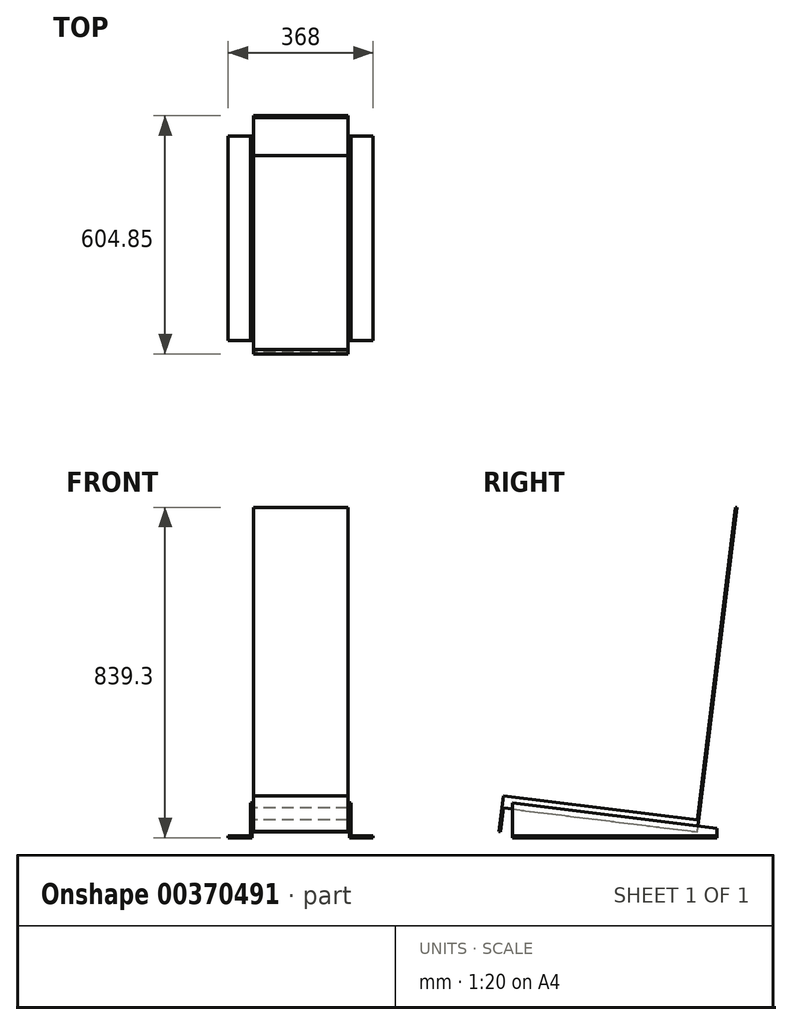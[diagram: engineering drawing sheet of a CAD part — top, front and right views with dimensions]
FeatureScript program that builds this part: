
annotation { "Feature Type Name" : "Feature", "Feature Type Description" : "" }
export const myFeature = defineFeature(function(context is Context, id is Id, definition is map)
    precondition{}
    {
        {
            var Q0;
            Q0=qCreatedBy(makeId("Right.planeOp"),FACE);
            var sketch = newSketch(context, id + "F0", { "sketchPlane" : qUnion([Q0])});
            skLineSegment(sketch, "E0", {"start": v(0, 0) * mm, "end": v(3.66, 29.78) * mm});
            skLineSegment(sketch, "E1", {"start": v(-492.62, 90.71) * mm, "end": v(-503.7, 0.49) * mm});
            skLineSegment(sketch, "E2", {"start": v(-503.7, 0.49) * mm, "end": v(-499.72, 0) * mm});
            skLineSegment(sketch, "E3", {"start": v(-499.72, 0) * mm, "end": v(-492.3, 60.45) * mm});
            skLineSegment(sketch, "E4", {"start": v(-492.3, 60.45) * mm, "end": v(0, 0) * mm});
            skLineSegment(sketch, "E5", {"start": v(-492.62, 90.71) * mm, "end": v(3.66, 29.78) * mm});
            skSolve(sketch);
        }
        {
            var Q0;
            Q0 = qSketchRegion(id + "F0", true);
            extrude(context, id + "F1", {"entities" : qUnion([Q0]), "depth" : 120 * mm});
        }
        {
            var Q0;
            Q0=makeQuery(id+"F1.opExtrude","CAP_FACE",FACE,{"disambiguationData":[OSD([sQuery(id+"F0.wireOp",EDGE,"E0"),sQuery(id+"F0.wireOp",EDGE,"E1"),sQuery(id+"F0.wireOp",EDGE,"E2"),sQuery(id+"F0.wireOp",EDGE,"E3"),sQuery(id+"F0.wireOp",EDGE,"E4"),sQuery(id+"F0.wireOp",EDGE,"E5")])],"isStart":false});
            var sketch = newSketch(context, id + "F2", { "sketchPlane" : qUnion([Q0])});
            skLineSegment(sketch, "E6", {"start": v(50, -15) * mm, "end": v(-470, -15) * mm});
            skLineSegment(sketch, "E7", {"start": v(-470, -15) * mm, "end": v(-470, 72.82) * mm});
            skLineSegment(sketch, "E8", {"start": v(-470, 72.82) * mm, "end": v(50, 8.97) * mm});
            skLineSegment(sketch, "E9", {"start": v(50, 8.97) * mm, "end": v(50, -15) * mm});
            skSolve(sketch);
        }
        {
            var Q0;
            {var subQ5=sQuery(id+"F2.wireOp",EDGE,"E6");Q0=makeQuery(id+"F2.imprint","IMPRINT",FACE,{"disambiguationData":[TD([[makeQuery(id+"F2.imprint","IMPRINT",EDGE,{"derivedFrom":subQ5}),-1.0]])]});}
            var Q1;
            {var subQ0=sQuery(id+"F2.wireOp",EDGE,"E8");var subQ1=sQuery(id+"F2.wireOp",EDGE,"E7");var subQ2=makeQuery(id+"F2.imprint","INTERSECT",VERTEX,{"derivedFrom":[subQ1,subQ0]});Q1=makeQuery(id+"F2.imprint","IMPRINT",FACE,{"disambiguationData":[TD([[makeQuery(id+"F2.imprint","IMPRINT",EDGE,{"disambiguationData":[TD([[subQ2,1.0]])],"derivedFrom":subQ1}),-1.0]])]});}
            extrude(context, id + "F3", {"entities" : qUnion([Q0, Q1]), "depth" : 60 * mm});
        }
        {
            var Q0;
            Q0=makeQuery(id+"F3.opExtrude","SWEPT_BODY",BODY,{"disambiguationData":[OSD([sQuery(id+"F2.wireOp",EDGE,"E6"),sQuery(id+"F2.wireOp",EDGE,"E7"),sQuery(id+"F2.wireOp",EDGE,"E8"),sQuery(id+"F2.wireOp",EDGE,"E9")])]});
            transform(context, id + "F4", {"entities" : qUnion([Q0]), "transformType" : TransformType.TRANSLATION_3D, "dx" : 4 * mm, "dy" : 0 * mm, "dz" : 0 * mm, "makeCopy" : false});
        }
        {
            var Q0;
            Q0=makeQuery(id+"F3.opExtrude","SWEPT_FACE",FACE,{"disambiguationData":[OSD([sQuery(id+"F2.wireOp",EDGE,"E7")])]});
            var Q1;
            Q1=makeQuery(id+"F3.opExtrude","CAP_FACE",FACE,{"disambiguationData":[OSD([sQuery(id+"F2.wireOp",EDGE,"E6"),sQuery(id+"F2.wireOp",EDGE,"E7"),sQuery(id+"F2.wireOp",EDGE,"E8"),sQuery(id+"F2.wireOp",EDGE,"E9")])],"isStart":false});
            var Q2;
            Q2=makeQuery(id+"F3.opExtrude","SWEPT_FACE",FACE,{"disambiguationData":[OSD([sQuery(id+"F2.wireOp",EDGE,"E8")])]});
            var Q3;
            Q3=makeQuery(id+"F3.opExtrude","SWEPT_FACE",FACE,{"disambiguationData":[OSD([sQuery(id+"F2.wireOp",EDGE,"E9")])]});
            shell(context, id + "F5", {"entities" : qUnion([Q0, Q1, Q2, Q3]), "thickness" : 4 * mm});
        }
        {
            var Q0;
            Q0=makeQuery(id+"F1.opExtrude","SWEPT_FACE",FACE,{"disambiguationData":[OSD([sQuery(id+"F0.wireOp",EDGE,"E5")])]});
            var sketch = newSketch(context, id + "F6", { "sketchPlane" : qUnion([Q0])});
            skLineSegment(sketch, "E10.bottom", {"start": v(120, 0) * mm, "end": v(0, 0) * mm});
            skLineSegment(sketch, "E10.top", {"start": v(120, -4) * mm, "end": v(0, -4) * mm});
            skLineSegment(sketch, "E10.left", {"start": v(120, 0) * mm, "end": v(120, -4) * mm});
            skLineSegment(sketch, "E10.right", {"start": v(0, 0) * mm, "end": v(0, -4) * mm});
            skSolve(sketch);
        }
        {
            var Q0;
            Q0 = qSketchRegion(id + "F6", true);
            extrude(context, id + "F7", {"entities" : qUnion([Q0]), "operationType" : NewBodyOperationType.ADD, "depth" : 800 * mm});
        }
        {
            var Q0;
            {var subQ0=sQuery(id+"F2.wireOp",EDGE,"E8");var subQ1=sQuery(id+"F2.wireOp",EDGE,"E7");var subQ2=makeQuery(id+"F2.imprint","INTERSECT",VERTEX,{"derivedFrom":[subQ1,subQ0]});Q0=makeQuery(id+"F2.imprint","IMPRINT",FACE,{"disambiguationData":[TD([[makeQuery(id+"F2.imprint","IMPRINT",EDGE,{"disambiguationData":[TD([[subQ2,1.0]])],"derivedFrom":subQ1}),-1.0]])]});}
            extrude(context, id + "F8", {"entities" : qUnion([Q0]), "depth" : 4 * mm});
        }
        {
            var Q0;
            Q0=makeQuery(id+"F3.opExtrude","SWEPT_BODY",BODY,{"disambiguationData":[OSD([sQuery(id+"F2.wireOp",EDGE,"E6"),sQuery(id+"F2.wireOp",EDGE,"E7"),sQuery(id+"F2.wireOp",EDGE,"E8"),sQuery(id+"F2.wireOp",EDGE,"E9")])]});
            var Q1;
            Q1=makeQuery(id+"F1.opExtrude","SWEPT_BODY",BODY,{"disambiguationData":[OSD([sQuery(id+"F0.wireOp",EDGE,"E0"),sQuery(id+"F0.wireOp",EDGE,"E1"),sQuery(id+"F0.wireOp",EDGE,"E2"),sQuery(id+"F0.wireOp",EDGE,"E3"),sQuery(id+"F0.wireOp",EDGE,"E4"),sQuery(id+"F0.wireOp",EDGE,"E5")])]});
            var Q2;
            Q2=qCreatedBy(makeId("Right.planeOp"),FACE);
            mirror(context, id + "F9", {"operationType" : NewBodyOperationType.ADD, "entities" : qUnion([Q0, Q1]), "mirrorPlane" : qUnion([Q2])});
        }
    });
